# Revit family: revitupgrade
name_source: partatom
category: Furniture
units: mm (PartAtom-declared; Revit-internal decimal feet)

## family parameters
Always vertical = Yes
Cut with Voids When Loaded = No
Enable Cutting in Views = No
OmniClass Number = 23.40.70.14.64.11
OmniClass Title = Office Furniture
Render Appearance Source = Family Geometry
Room Calculation Point = No
Shared = No
Work Plane-Based = No

## types (1)
- Straight Bench
    Assembly Code = E2020200
    Default Elevation = 0 mm  [stored 0 ft]
    Description = Just like learning, furniture shouldn’t be forced.  Flowform® is refreshing in that way.  They feature deliberate organic shapes with soft radii and rounded edging.
    Glide = SmithSystem_Plastic_Black
    Manufacturer = Smith System
    Release Date = June 2023
    Style Number(s) = SMSFS55004
    URL = https://www.steelcase.com

note: [stored X ft] marks values corroborated as IEEE doubles in the binary element streams (Revit-internal decimal feet)

## geometry (parser evidence)
native form markers: Sweep x2
no freeform markers — native parametric forms only
